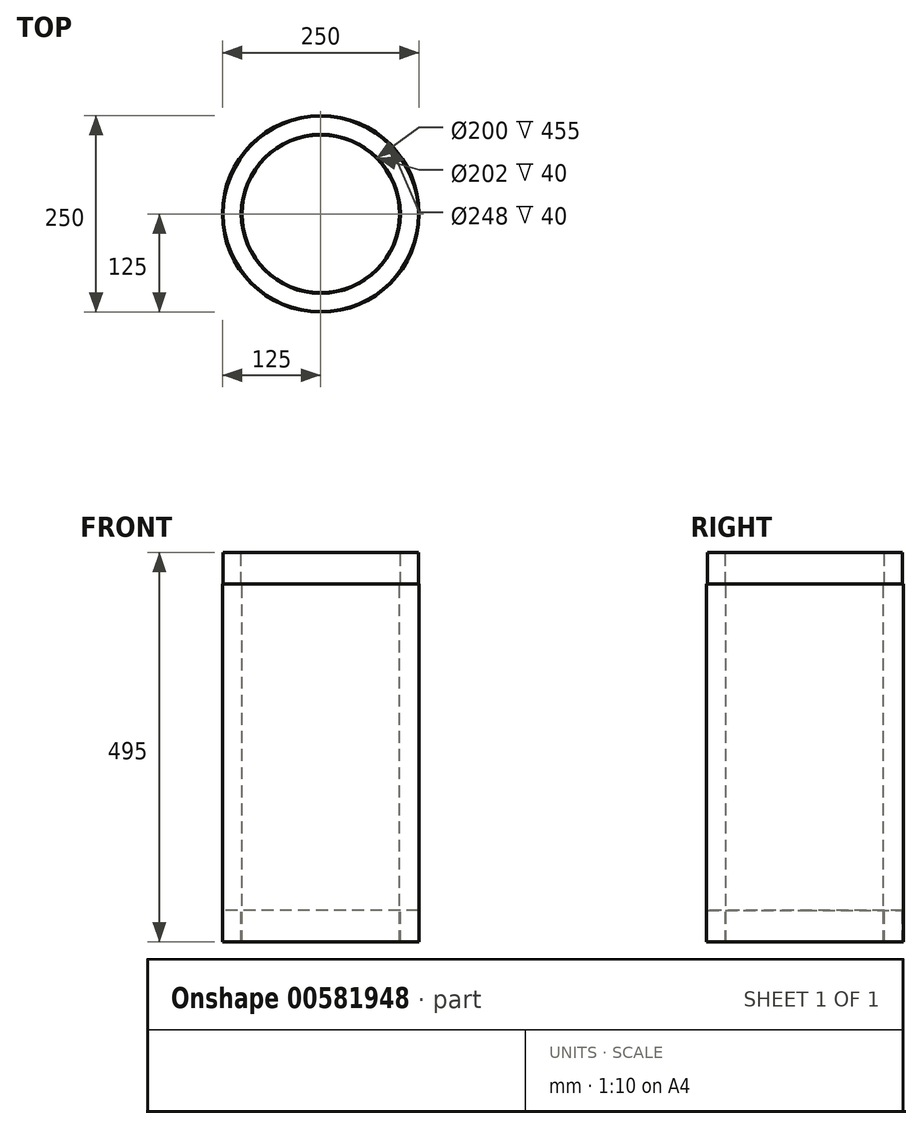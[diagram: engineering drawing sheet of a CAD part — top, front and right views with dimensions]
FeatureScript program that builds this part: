
annotation { "Feature Type Name" : "Feature", "Feature Type Description" : "" }
export const myFeature = defineFeature(function(context is Context, id is Id, definition is map)
    precondition{}
    {
        {
            var Q0;
            Q0=qCreatedBy(makeId("Front.planeOp"),FACE);
            var sketch = newSketch(context, id + "F0", { "sketchPlane" : qUnion([Q0])});
            skLineSegment(sketch, "E0", {"start": v(0, 345.75) * mm, "end": v(0, -558.03) * mm, "construction": true});
            skLineSegment(sketch, "E1", {"start": v(-100, -518.84) * mm, "end": v(-100, -63.84) * mm});
            skLineSegment(sketch, "E2", {"start": v(-100, -63.84) * mm, "end": v(-101, -63.84) * mm});
            skLineSegment(sketch, "E3", {"start": v(-101, -63.84) * mm, "end": v(-101, -23.84) * mm});
            skLineSegment(sketch, "E4", {"start": v(-101, -23.84) * mm, "end": v(-124, -23.84) * mm});
            skLineSegment(sketch, "E5", {"start": v(-124, -23.84) * mm, "end": v(-124, -63.84) * mm});
            skLineSegment(sketch, "E6", {"start": v(-124, -63.84) * mm, "end": v(-125, -63.84) * mm});
            skLineSegment(sketch, "E7", {"start": v(-125, -63.84) * mm, "end": v(-125, -518.84) * mm});
            skLineSegment(sketch, "E8", {"start": v(-125, -518.84) * mm, "end": v(-124, -518.84) * mm});
            skLineSegment(sketch, "E9", {"start": v(-124, -518.84) * mm, "end": v(-124, -478.84) * mm});
            skLineSegment(sketch, "E10", {"start": v(-124, -478.84) * mm, "end": v(-101, -478.84) * mm});
            skLineSegment(sketch, "E11", {"start": v(-101, -478.84) * mm, "end": v(-101, -518.84) * mm});
            skLineSegment(sketch, "E12", {"start": v(-101, -518.84) * mm, "end": v(-100, -518.84) * mm});
            skSolve(sketch);
        }
        {
            var Q0;
            Q0=qSketchRegion(id+"F0",true);
            var Q1;
            Q1=sQuery(id+"F0.wireOp",EDGE,"E0");
            revolve(context, id + "F1", {"entities" : qUnion([Q0]), "axis" : qUnion([Q1]), "revolveType" : RevolveType.FULL});
        }
    });
